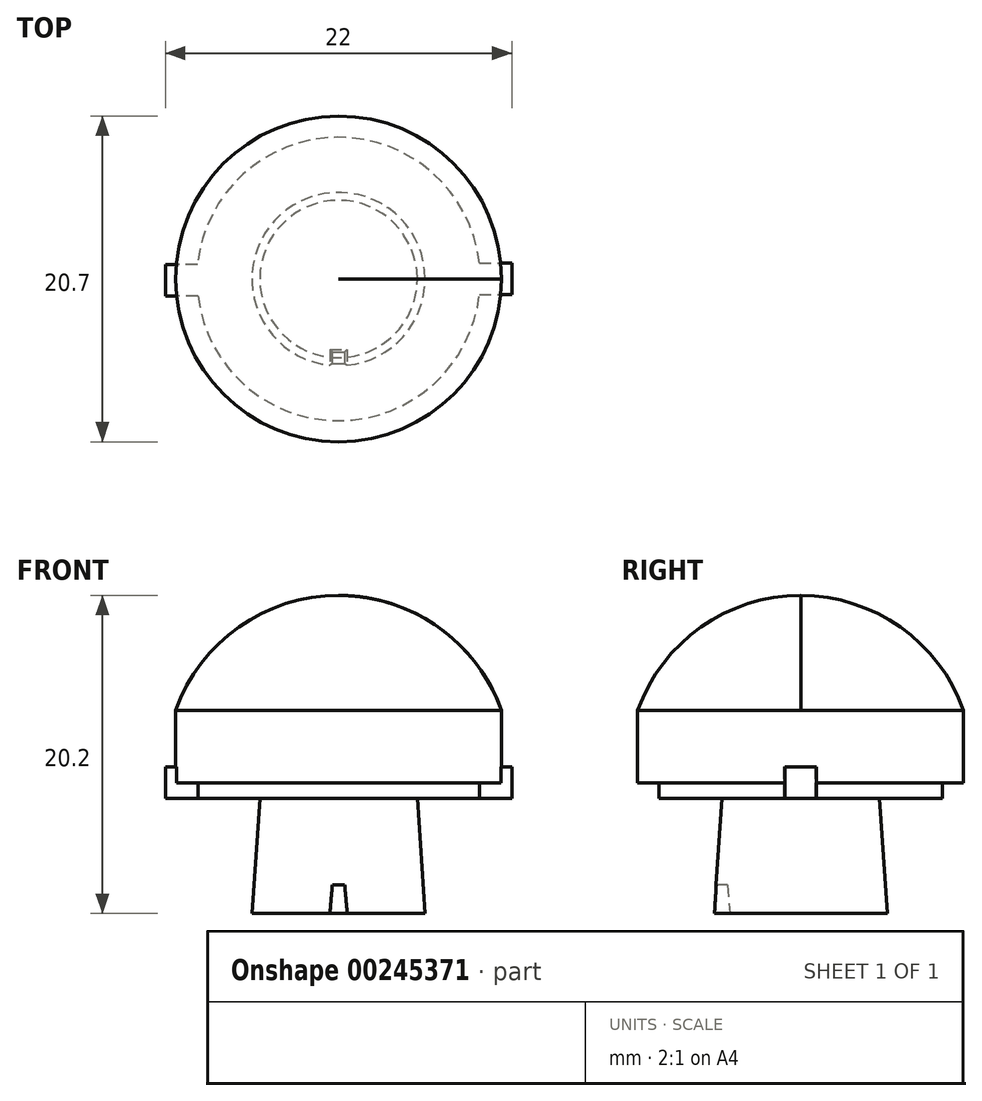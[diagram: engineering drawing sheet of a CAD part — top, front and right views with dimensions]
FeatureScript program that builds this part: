
annotation { "Feature Type Name" : "Feature", "Feature Type Description" : "" }
export const myFeature = defineFeature(function(context is Context, id is Id, definition is map)
    precondition{}
    {
        {
            var Q0;
            Q0=qCreatedBy(makeId("Front.planeOp"),FACE);
            var sketch = newSketch(context, id + "F0", { "sketchPlane" : qUnion([Q0])});
            skLineSegment(sketch, "E0", {"start": v(0, 0) * mm, "end": v(5.5, 0) * mm});
            skLineSegment(sketch, "E1", {"start": v(0, 20.2) * mm, "end": v(16.44, 20.2) * mm, "construction": true});
            skLineSegment(sketch, "E2", {"start": v(10.35, 7.3) * mm, "end": v(10.35, 0) * mm, "construction": true});
            skLineSegment(sketch, "E3", {"start": v(10.35, 7.3) * mm, "end": v(0, 7.3) * mm, "construction": true});
            skLineSegment(sketch, "E4", {"start": v(0, 7.3) * mm, "end": v(5, 7.3) * mm});
            skLineSegment(sketch, "E5", {"start": v(5, 7.3) * mm, "end": v(5.5, 0) * mm});
            skLineSegment(sketch, "E6", {"start": v(5, 7.3) * mm, "end": v(9, 7.3) * mm});
            skLineSegment(sketch, "E7", {"start": v(9, 7.3) * mm, "end": v(9, 8.3) * mm});
            skLineSegment(sketch, "E8", {"start": v(9, 7.3) * mm, "end": v(11, 7.3) * mm, "construction": true});
            skLineSegment(sketch, "E9", {"start": v(11, 7.3) * mm, "end": v(11, 9.3) * mm, "construction": true});
            skLineSegment(sketch, "E10", {"start": v(9, 8.3) * mm, "end": v(10.35, 8.3) * mm});
            skLineSegment(sketch, "E11", {"start": v(10.35, 8.3) * mm, "end": v(10.35, 9.3) * mm});
            skLineSegment(sketch, "E12", {"start": v(10.35, 9.3) * mm, "end": v(11, 9.3) * mm, "construction": true});
            skLineSegment(sketch, "E13", {"start": v(10.35, 9.3) * mm, "end": v(10.35, 12.9) * mm});
            skLineSegment(sketch, "E14", {"start": v(0, 12.9) * mm, "end": v(-10.35, 12.9) * mm, "construction": true});
            skLineSegment(sketch, "E15", {"start": v(0, 12.9) * mm, "end": v(10.35, 12.9) * mm, "construction": true});
            skArc(sketch, "E16", {"start": v(10.35, 12.9) * mm, "mid": v(6.33, 18.2) * mm, "end": v(0, 20.2) * mm});
            skLineSegment(sketch, "E17", {"start": v(0, 0) * mm, "end": v(0, 20.2) * mm});
            skSolve(sketch);
        }
        {
            var Q0;
            Q0 = qSketchRegion(id + "F0", true);
            extrude(context, id + "F1", {"entities" : qUnion([Q0]), "depth" : 0.01 * mm});
        }
        {
            var Q0;
            Q0=makeQuery(id+"F1.opExtrude","CAP_FACE",FACE,{"disambiguationData":[OSD([sQuery(id+"F0.wireOp",EDGE,"E0"),sQuery(id+"F0.wireOp",EDGE,"E5"),sQuery(id+"F0.wireOp",EDGE,"E6"),sQuery(id+"F0.wireOp",EDGE,"E7"),sQuery(id+"F0.wireOp",EDGE,"E10"),sQuery(id+"F0.wireOp",EDGE,"E11"),sQuery(id+"F0.wireOp",EDGE,"E13"),sQuery(id+"F0.wireOp",EDGE,"E16"),sQuery(id+"F0.wireOp",EDGE,"74306cc8-111f-4a76-b4a3-b401b2c3296c0.MirrorCS"),sQuery(id+"F0.wireOp",EDGE,"74306cc8-111f-4a76-b4a3-b401b2c3296c2.MirrorCS"),sQuery(id+"F0.wireOp",EDGE,"74306cc8-111f-4a76-b4a3-b401b2c3296c3.MirrorCS"),sQuery(id+"F0.wireOp",EDGE,"74306cc8-111f-4a76-b4a3-b401b2c3296c6.MirrorCS"),sQuery(id+"F0.wireOp",EDGE,"74306cc8-111f-4a76-b4a3-b401b2c3296c7.MirrorCS"),sQuery(id+"F0.wireOp",EDGE,"74306cc8-111f-4a76-b4a3-b401b2c3296c9.MirrorCS"),sQuery(id+"F0.wireOp",EDGE,"74306cc8-111f-4a76-b4a3-b401b2c3296c13.MirrorCS")])],"isStart":false});
            var Q1;
            Q1=makeQuery(id+"F1.opExtrude","CAP_EDGE",EDGE,{"disambiguationData":[OSD([sQuery(id+"F0.wireOp",EDGE,"E17")])],"isStart":false});
            revolve(context, id + "F2", {"operationType" : NewBodyOperationType.ADD, "entities" : qUnion([Q0]), "axis" : qUnion([Q1]), "revolveType" : RevolveType.FULL});
        }
        {
            var Q0;
            {var subQ0=sQuery(id+"F0.wireOp",EDGE,"E0");Q0=makeQuery(id+"F2.boolean.opBoolean","MERGE",FACE,{"derivedFrom":[makeQuery(id+"F1.opExtrude","SWEPT_FACE",FACE,{"disambiguationData":[OSD([subQ0])]}),makeQuery(id+"F2.opRevolve","SWEPT_FACE",FACE,{"disambiguationData":[OSD([subQ0])]})]});}
            var sketch = newSketch(context, id + "F3", { "sketchPlane" : qUnion([Q0])});
            skCircle(sketch, "E18", {"center": v(0, 0) * mm, "radius": 6 * mm, "construction": true});
            skLineSegment(sketch, "E19", {"start": v(0, 6) * mm, "end": v(0, 4.5) * mm, "construction": true});
            skLineSegment(sketch, "E20", {"start": v(0, 4.5) * mm, "end": v(0.55, 4.5) * mm});
            skLineSegment(sketch, "E21", {"start": v(0.55, 4.5) * mm, "end": v(0.55, 5.97) * mm});
            skLineSegment(sketch, "E22", {"start": v(0, 4.5) * mm, "end": v(-0.55, 4.5) * mm});
            skLineSegment(sketch, "E23", {"start": v(-0.55, 4.5) * mm, "end": v(-0.55, 5.97) * mm});
            skLineSegment(sketch, "E24", {"start": v(-0.55, 5.97) * mm, "end": v(0.55, 5.97) * mm});
            skSolve(sketch);
        }
        {
            var Q0;
            Q0 = qSketchRegion(id + "F3", true);
            extrude(context, id + "F4", {"entities" : qUnion([Q0]), "operationType" : NewBodyOperationType.REMOVE, "oppositeDirection" : true, "depth" : 1.8 * mm});
        }
        {
            var Q0;
            Q0=makeQuery(id+"F4.boolean.opBoolean","COPY",EDGE,{"derivedFrom":makeQuery(id+"F4.opExtrude","CAP_EDGE",EDGE,{"disambiguationData":[OSD([sQuery(id+"F3.wireOp",EDGE,"E23")])],"isStart":false})});
            var Q1;
            Q1=makeQuery(id+"F4.boolean.opBoolean","COPY",EDGE,{"derivedFrom":makeQuery(id+"F4.opExtrude","CAP_EDGE",EDGE,{"disambiguationData":[OSD([sQuery(id+"F3.wireOp",EDGE,"E21")])],"isStart":false})});
            var Q2;
            Q2=makeQuery(id+"F4.boolean.opBoolean","COPY",EDGE,{"derivedFrom":makeQuery(id+"F4.opExtrude","CAP_EDGE",EDGE,{"disambiguationData":[OSD([sQuery(id+"F3.wireOp",EDGE,"E20"),sQuery(id+"F3.wireOp",EDGE,"E22")])],"isStart":false})});
            chamfer(context, id + "F5", {"entities" : qUnion([Q0, Q1, Q2]), "chamferType" : ChamferType.OFFSET_ANGLE, "width" : 1.8 * mm, "oppositeDirection" : false, "angle" : 5 * degree, "tangentPropagation" : true});
        }
        {
            var Q0;
            Q0=qCreatedBy(makeId("Front.planeOp"),FACE);
            var sketch = newSketch(context, id + "F6", { "sketchPlane" : qUnion([Q0])});
            skLineSegment(sketch, "E25", {"start": v(10.35, 9.3) * mm, "end": v(11, 9.3) * mm});
            skLineSegment(sketch, "E26", {"start": v(11, 9.3) * mm, "end": v(11, 7.3) * mm});
            skLineSegment(sketch, "E27", {"start": v(11, 7.3) * mm, "end": v(9, 7.3) * mm});
            skLineSegment(sketch, "E28", {"start": v(9, 7.3) * mm, "end": v(9, 8.3) * mm});
            skLineSegment(sketch, "E29", {"start": v(9, 8.3) * mm, "end": v(10.35, 8.3) * mm});
            skLineSegment(sketch, "E30", {"start": v(10.35, 8.3) * mm, "end": v(10.35, 9.3) * mm});
            skLineSegment(sketch, "E31.MirrorCS", {"start": v(-10.35, 9.3) * mm, "end": v(-11, 9.3) * mm});
            skLineSegment(sketch, "E32.MirrorCS", {"start": v(-10.35, 8.3) * mm, "end": v(-10.35, 9.3) * mm});
            skLineSegment(sketch, "E33.MirrorCS", {"start": v(-9, 7.3) * mm, "end": v(-9, 8.3) * mm});
            skLineSegment(sketch, "E34.MirrorCS", {"start": v(-11, 7.3) * mm, "end": v(-9, 7.3) * mm});
            skLineSegment(sketch, "E35.MirrorCS", {"start": v(-11, 9.3) * mm, "end": v(-11, 7.3) * mm});
            skLineSegment(sketch, "E36.MirrorCS", {"start": v(-9, 8.3) * mm, "end": v(-10.35, 8.3) * mm});
            skSolve(sketch);
        }
        {
            var Q0;
            Q0 = qSketchRegion(id + "F6", true);
            extrude(context, id + "F7", {"entities" : qUnion([Q0]), "operationType" : NewBodyOperationType.ADD, "depth" : 0.1 * mm});
        }
        {
            var Q0;
            Q0=makeQuery(id+"F7.opExtrude","SWEPT_FACE",FACE,{"disambiguationData":[OSD([sQuery(id+"F6.wireOp",EDGE,"E26")])]});
            var sketch = newSketch(context, id + "F8", { "sketchPlane" : qUnion([Q0])});
            skLineSegment(sketch, "E37.bottom", {"start": v(-1, 9.3) * mm, "end": v(0, 9.3) * mm});
            skLineSegment(sketch, "E37.top", {"start": v(-1, 7.3) * mm, "end": v(0, 7.3) * mm});
            skLineSegment(sketch, "E37.left", {"start": v(-1, 9.3) * mm, "end": v(-1, 7.3) * mm});
            skLineSegment(sketch, "E38.MirrorCS", {"start": v(1, 9.3) * mm, "end": v(1, 7.3) * mm});
            skLineSegment(sketch, "E39.MirrorCS", {"start": v(1, 7.3) * mm, "end": v(0, 7.3) * mm});
            skLineSegment(sketch, "E40.MirrorCS", {"start": v(1, 9.3) * mm, "end": v(0, 9.3) * mm});
            skSolve(sketch);
        }
        {
            var Q0;
            Q0 = qSketchRegion(id + "F8", true);
            extrude(context, id + "F9", {"entities" : qUnion([Q0]), "operationType" : NewBodyOperationType.ADD, "endBound" : BoundingType.UP_TO_NEXT, "oppositeDirection" : true, "depth" : 25 * mm});
        }
        {
            var Q0;
            Q0=makeQuery(id+"F7.opExtrude","SWEPT_FACE",FACE,{"disambiguationData":[OSD([sQuery(id+"F6.wireOp",EDGE,"E35.MirrorCS")])]});
            var sketch = newSketch(context, id + "F10", { "sketchPlane" : qUnion([Q0])});
            skLineSegment(sketch, "E41.bottom", {"start": v(0.1, 9.3) * mm, "end": v(-0.9, 9.3) * mm});
            skLineSegment(sketch, "E41.right", {"start": v(-0.9, 9.3) * mm, "end": v(-0.9, 7.3) * mm});
            skLineSegment(sketch, "E42", {"start": v(-0.9, 7.3) * mm, "end": v(0.1, 7.3) * mm});
            skLineSegment(sketch, "E43", {"start": v(1.1, 7.3) * mm, "end": v(0.1, 7.3) * mm});
            skLineSegment(sketch, "E44", {"start": v(0.1, 9.3) * mm, "end": v(1.1, 9.3) * mm});
            skLineSegment(sketch, "E45", {"start": v(1.1, 9.3) * mm, "end": v(1.1, 7.3) * mm});
            skSolve(sketch);
        }
        {
            var Q0;
            Q0 = qSketchRegion(id + "F10", true);
            extrude(context, id + "F11", {"entities" : qUnion([Q0]), "operationType" : NewBodyOperationType.ADD, "endBound" : BoundingType.UP_TO_NEXT, "oppositeDirection" : true, "depth" : 25 * mm});
        }
    });
